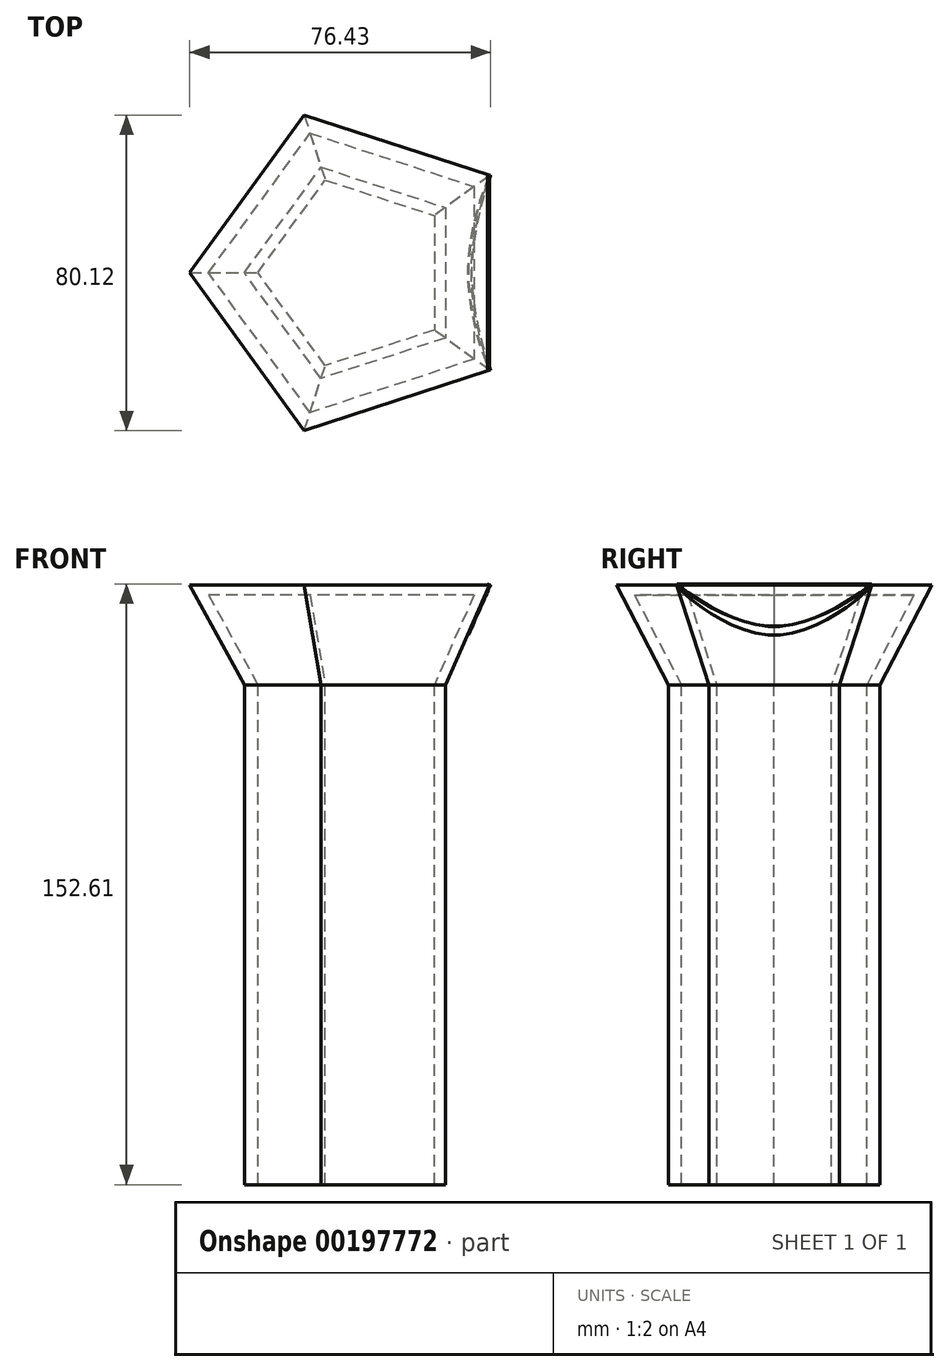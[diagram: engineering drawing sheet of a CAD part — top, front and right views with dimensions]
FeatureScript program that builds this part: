
annotation { "Feature Type Name" : "Feature", "Feature Type Description" : "" }
export const myFeature = defineFeature(function(context is Context, id is Id, definition is map)
    precondition{}
    {
        {
            var Q0;
            Q0=qCreatedBy(makeId("Top.planeOp"),FACE);
            var sketch = newSketch(context, id + "F0", { "sketchPlane" : qUnion([Q0])});
            skCircle(sketch, "E0.cCircle", {"center": v(0, 0) * mm, "radius": 22.83 * mm, "construction": true});
            skLineSegment(sketch, "E0.0", {"start": v(22.83, 16.59) * mm, "end": v(22.83, -16.59) * mm});
            skLineSegment(sketch, "E0.1", {"start": v(22.83, -16.59) * mm, "end": v(-8.72, -26.84) * mm});
            skLineSegment(sketch, "E0.2", {"start": v(-8.72, -26.84) * mm, "end": v(-28.22, 0) * mm});
            skLineSegment(sketch, "E0.3", {"start": v(-28.22, 0) * mm, "end": v(-8.72, 26.84) * mm});
            skLineSegment(sketch, "E0.4", {"start": v(-8.72, 26.84) * mm, "end": v(22.83, 16.59) * mm});
            skPoint(sketch, "E0.0.midPoint", {"position": v(22.83, 0) * mm});
            skSolve(sketch);
        }
        {
            var Q0;
            Q0=qCreatedBy(makeId("Top.planeOp"),FACE);
            cPlane(context, id + "F1", {"entities" : qUnion([Q0]), "cplaneType" : CPlaneType.OFFSET, "offset" : 25.4 * mm, "width" : 152.4 * mm, "height" : 152.4 * mm});
        }
        {
            var Q0;
            Q0=qCreatedBy(id+"F1.planeOp",FACE);
            var sketch = newSketch(context, id + "F2", { "sketchPlane" : qUnion([Q0])});
            skCircle(sketch, "E1.cCircle", {"center": v(0, 0) * mm, "radius": 34.08 * mm, "construction": true});
            skLineSegment(sketch, "E1.0", {"start": v(34.08, 24.76) * mm, "end": v(34.08, -24.76) * mm});
            skLineSegment(sketch, "E1.1", {"start": v(34.08, -24.76) * mm, "end": v(-13.02, -40.06) * mm});
            skLineSegment(sketch, "E1.2", {"start": v(-13.02, -40.06) * mm, "end": v(-42.12, 0) * mm});
            skLineSegment(sketch, "E1.3", {"start": v(-42.12, 0) * mm, "end": v(-13.02, 40.06) * mm});
            skLineSegment(sketch, "E1.4", {"start": v(-13.02, 40.06) * mm, "end": v(34.08, 24.76) * mm});
            skPoint(sketch, "E1.0.midPoint", {"position": v(34.08, 0) * mm});
            skSolve(sketch);
        }
        {
            var Q0;
            Q0=makeQuery(id+"F2.imprint","IMPRINT",FACE,{"disambiguationData":[TD([[makeQuery(id+"F2.imprint","IMPRINT",EDGE,{"derivedFrom":sQuery(id+"F2.wireOp",EDGE,"E1.0")}),-1.0]])]});
            var Q1;
            Q1=makeQuery(id+"F0.imprint","IMPRINT",FACE,{"disambiguationData":[TD([[makeQuery(id+"F0.imprint","IMPRINT",EDGE,{"derivedFrom":sQuery(id+"F0.wireOp",EDGE,"E0.0")}),-1.0]])]});
            loft(context, id + "F3", {"sheetProfilesArray" : [{ "sheetProfileEntities" : qUnion([Q0]) }, { "sheetProfileEntities" : qUnion([Q1]) }]});
        }
        {
            var Q0;
            Q0=makeQuery(id+"F3.opLoft","CAP_FACE",FACE,{"disambiguationData":[OSD([makeQuery(id+"F0.imprint","IMPRINT",FACE,{"disambiguationData":[TD([[makeQuery(id+"F0.imprint","IMPRINT",EDGE,{"derivedFrom":sQuery(id+"F0.wireOp",EDGE,"E0.0")}),-1.0]])]})])],"isStart":true});
            shell(context, id + "F4", {"entities" : qUnion([Q0]), "thickness" : 2.54 * mm});
        }
        {
            var Q0;
            Q0=makeQuery(id+"F3.opLoft","CAP_FACE",FACE,{"disambiguationData":[OSD([makeQuery(id+"F0.imprint","IMPRINT",FACE,{"disambiguationData":[TD([[makeQuery(id+"F0.imprint","IMPRINT",EDGE,{"derivedFrom":sQuery(id+"F0.wireOp",EDGE,"E0.0")}),-1.0]])]})])],"isStart":true});
            extrude(context, id + "F5", {"entities" : qUnion([Q0]), "operationType" : NewBodyOperationType.ADD, "depth" : 127 * mm});
        }
        {
            var Q0;
            Q0=makeQuery(id+"F3.opLoft","SWEPT_FACE",FACE,{"disambiguationData":[OSD([sQuery(id+"F0.wireOp",EDGE,"E0.0"),sQuery(id+"F0.wireOp",EDGE,"E0.1"),sQuery(id+"F0.wireOp",EDGE,"E0.4"),sQuery(id+"F2.wireOp",EDGE,"E1.0"),sQuery(id+"F2.wireOp",EDGE,"E1.1"),sQuery(id+"F2.wireOp",EDGE,"E1.4")])]});
            var sketch = newSketch(context, id + "F6", { "sketchPlane" : qUnion([Q0])});
            skFitSpline(sketch, "E2", {"points": [v(24.76, 37.02) * mm, v(0, 23.15) * mm, v(-24.76, 37.02) * mm, v(0, 25.54) * mm, v(24.76, 37.02) * mm]});
            skFitSpline(sketch, "E3", {"points": [v(24.76, 37.02) * mm, v(0, 17.25) * mm, v(-24.76, 37.02) * mm, v(0, 29.72) * mm, v(24.76, 37.02) * mm]});
            skSolve(sketch);
        }
        {
            var Q0;
            {var subQ1=sQuery(id+"F6.wireOp",EDGE,"E2");var subQ2=sQuery(id+"F2.wireOp",EDGE,"E1.4");var subQ3=sQuery(id+"F2.wireOp",EDGE,"E1.1");var subQ4=sQuery(id+"F2.wireOp",EDGE,"E1.0");var subQ5=makeQuery(id+"F3.opLoft","MID_CAP_EDGE",EDGE,{"disambiguationData":[OSD([subQ4,subQ3,subQ2])],"capPos":0.0});var subQ13=makeQuery(id+"F6.imprint","INTERSECT",VERTEX,{"disambiguationData":[OD(0.0)],"derivedFrom":[subQ5,subQ1]});Q0=makeQuery(id+"F6.imprint","IMPRINT",FACE,{"disambiguationData":[TD([[makeQuery(id+"F6.imprint","IMPRINT",EDGE,{"disambiguationData":[TD([[subQ13,-1.0]])],"derivedFrom":subQ1}),-1.0]])]});}
            extrude(context, id + "F7", {"entities" : qUnion([Q0]), "operationType" : NewBodyOperationType.ADD, "depth" : 0.25 * mm});
        }
        {
            var Q0;
            {var subQ0=sQuery(id+"F0.wireOp",EDGE,"E0.4");var subQ2=sQuery(id+"F0.wireOp",EDGE,"E0.0");var subQ3=sQuery(id+"F2.wireOp",EDGE,"E1.1");var subQ4=sQuery(id+"F2.wireOp",EDGE,"E1.0");var subQ6=sQuery(id+"F0.wireOp",EDGE,"E0.1");var subQ7=sQuery(id+"F2.wireOp",EDGE,"E1.4");Q0=makeQuery(id+"F7.boolean.opBoolean","SPLIT",FACE,{"disambiguationData":[TD([makeQuery(id+"F5.opExtrude","SWEPT_FACE",FACE,{"disambiguationData":[OSD([subQ2,subQ6,subQ0]),TDD([makeQuery(id+"F3.opLoft","MID_CAP_EDGE",EDGE,{"disambiguationData":[OSD([subQ2,subQ6,subQ0])],"capPos":1.0})])]})])],"derivedFrom":makeQuery(id+"F3.opLoft","SWEPT_FACE",FACE,{"disambiguationData":[OSD([subQ2,subQ6,subQ0,subQ4,subQ3,subQ7])]})});}
            var Q1;
            {var subQ0=sQuery(id+"F2.wireOp",EDGE,"E1.1");var subQ1=sQuery(id+"F2.wireOp",EDGE,"E1.0");var subQ2=sQuery(id+"F2.wireOp",EDGE,"E1.4");var subQ4=sQuery(id+"F6.wireOp",EDGE,"E2");var subQ5=makeQuery(id+"F3.opLoft","MID_CAP_EDGE",EDGE,{"disambiguationData":[OSD([subQ1,subQ0,subQ2])],"capPos":0.0});var subQ6=sQuery(id+"F0.wireOp",EDGE,"E0.1");var subQ7=sQuery(id+"F0.wireOp",EDGE,"E0.0");var subQ8=makeQuery(id+"F6.imprint","INTERSECT",VERTEX,{"disambiguationData":[OD(0.0)],"derivedFrom":[subQ5,subQ4]});var subQ10=sQuery(id+"F0.wireOp",EDGE,"E0.4");Q1=makeQuery(id+"F7.boolean.opBoolean","SPLIT",FACE,{"disambiguationData":[TD([makeQuery(id+"F7.opExtrude","SWEPT_FACE",FACE,{"disambiguationData":[OSD([subQ4]),TDD([makeQuery(id+"F6.imprint","IMPRINT",EDGE,{"disambiguationData":[TD([[subQ8,-1.0]])],"derivedFrom":subQ4})])]})])],"derivedFrom":makeQuery(id+"F3.opLoft","SWEPT_FACE",FACE,{"disambiguationData":[OSD([subQ7,subQ6,subQ10,subQ1,subQ0,subQ2])]})});}
            extrude(context, id + "F8", {"entities" : qUnion([Q0, Q1]), "operationType" : NewBodyOperationType.ADD, "oppositeDirection" : true, "depth" : 0.5 * mm});
        }
    });
